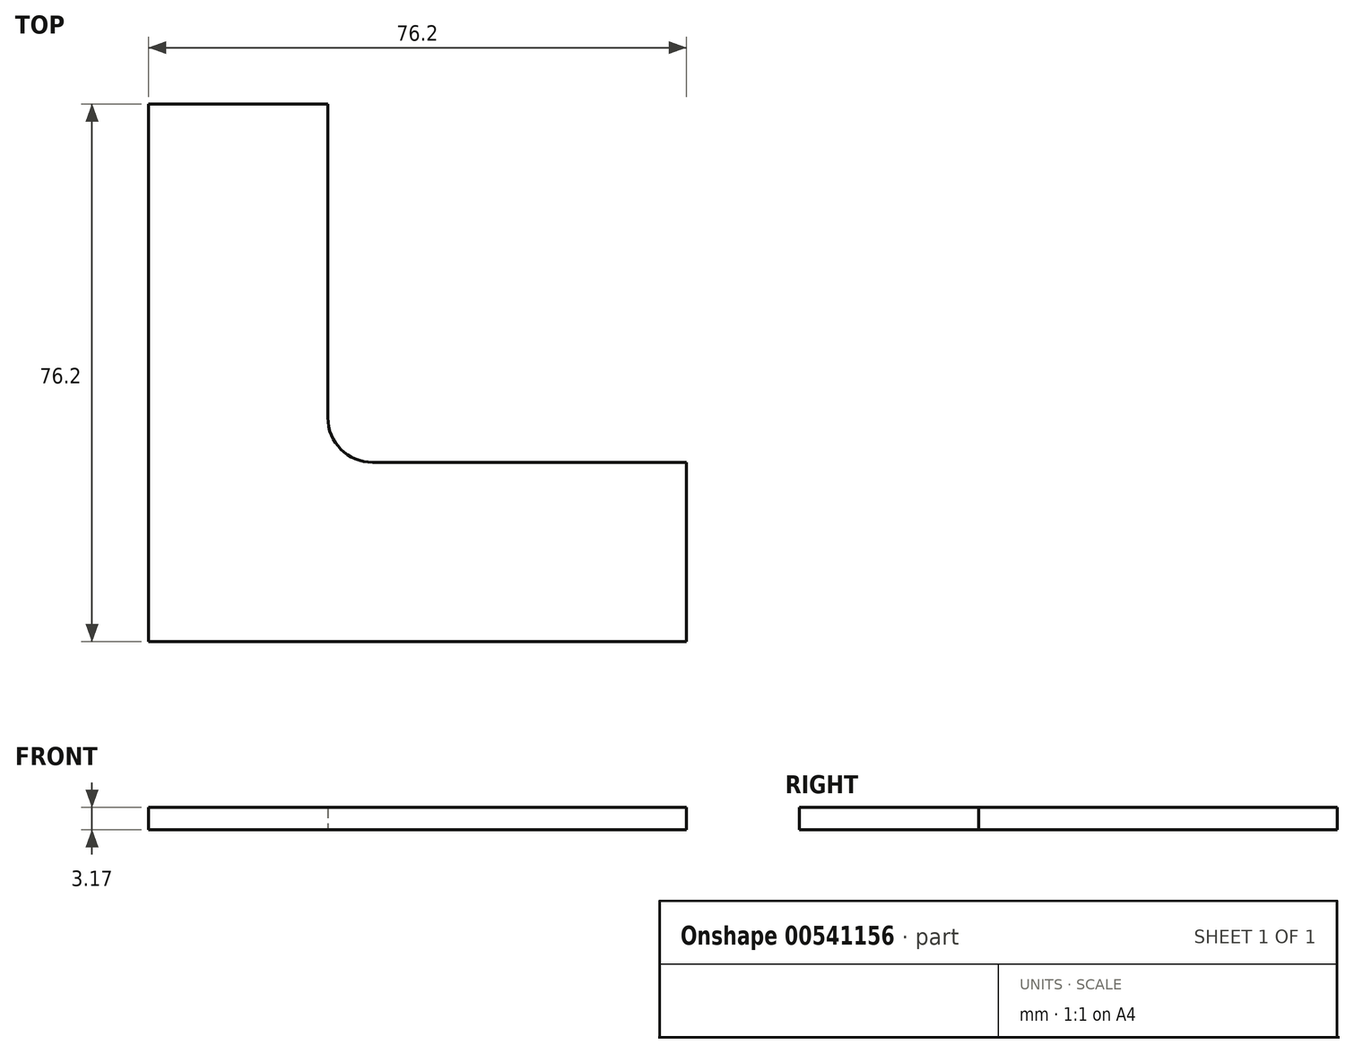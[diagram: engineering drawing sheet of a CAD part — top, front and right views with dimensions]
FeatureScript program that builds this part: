
annotation { "Feature Type Name" : "Feature", "Feature Type Description" : "" }
export const myFeature = defineFeature(function(context is Context, id is Id, definition is map)
    precondition{}
    {
        {
            var Q0;
            Q0=qCreatedBy(makeId("Top.planeOp"),FACE);
            var sketch = newSketch(context, id + "F0", { "sketchPlane" : qUnion([Q0])});
            skLineSegment(sketch, "E0", {"start": v(0, 0) * mm, "end": v(0, 76.2) * mm});
            skLineSegment(sketch, "E1", {"start": v(0, 0) * mm, "end": v(76.2, 0) * mm});
            skLineSegment(sketch, "E2", {"start": v(76.2, 0) * mm, "end": v(76.2, 25.4) * mm});
            skLineSegment(sketch, "E3", {"start": v(76.2, 25.4) * mm, "end": v(31.75, 25.4) * mm});
            skLineSegment(sketch, "E4", {"start": v(0, 76.2) * mm, "end": v(25.4, 76.2) * mm});
            skLineSegment(sketch, "E5", {"start": v(25.4, 76.2) * mm, "end": v(25.4, 31.75) * mm});
            skPoint(sketch, "E6.visualSharp", {"position": v(25.4, 25.4) * mm});
            skArc(sketch, "E6.filletArc", {"start": v(25.4, 31.75) * mm, "mid": v(27.26, 27.26) * mm, "end": v(31.75, 25.4) * mm});
            skSolve(sketch);
        }
        {
            var Q0;
            Q0=makeQuery(id+"F0.imprint","IMPRINT",FACE,{"disambiguationData":[TD([[makeQuery(id+"F0.imprint","IMPRINT",EDGE,{"derivedFrom":sQuery(id+"F0.wireOp",EDGE,"E0")}),-1.0]])]});
            extrude(context, id + "F1", {"entities" : qUnion([Q0]), "depth" : 3.17 * mm, "offsetDistance" : 25.4 * mm});
        }
    });
